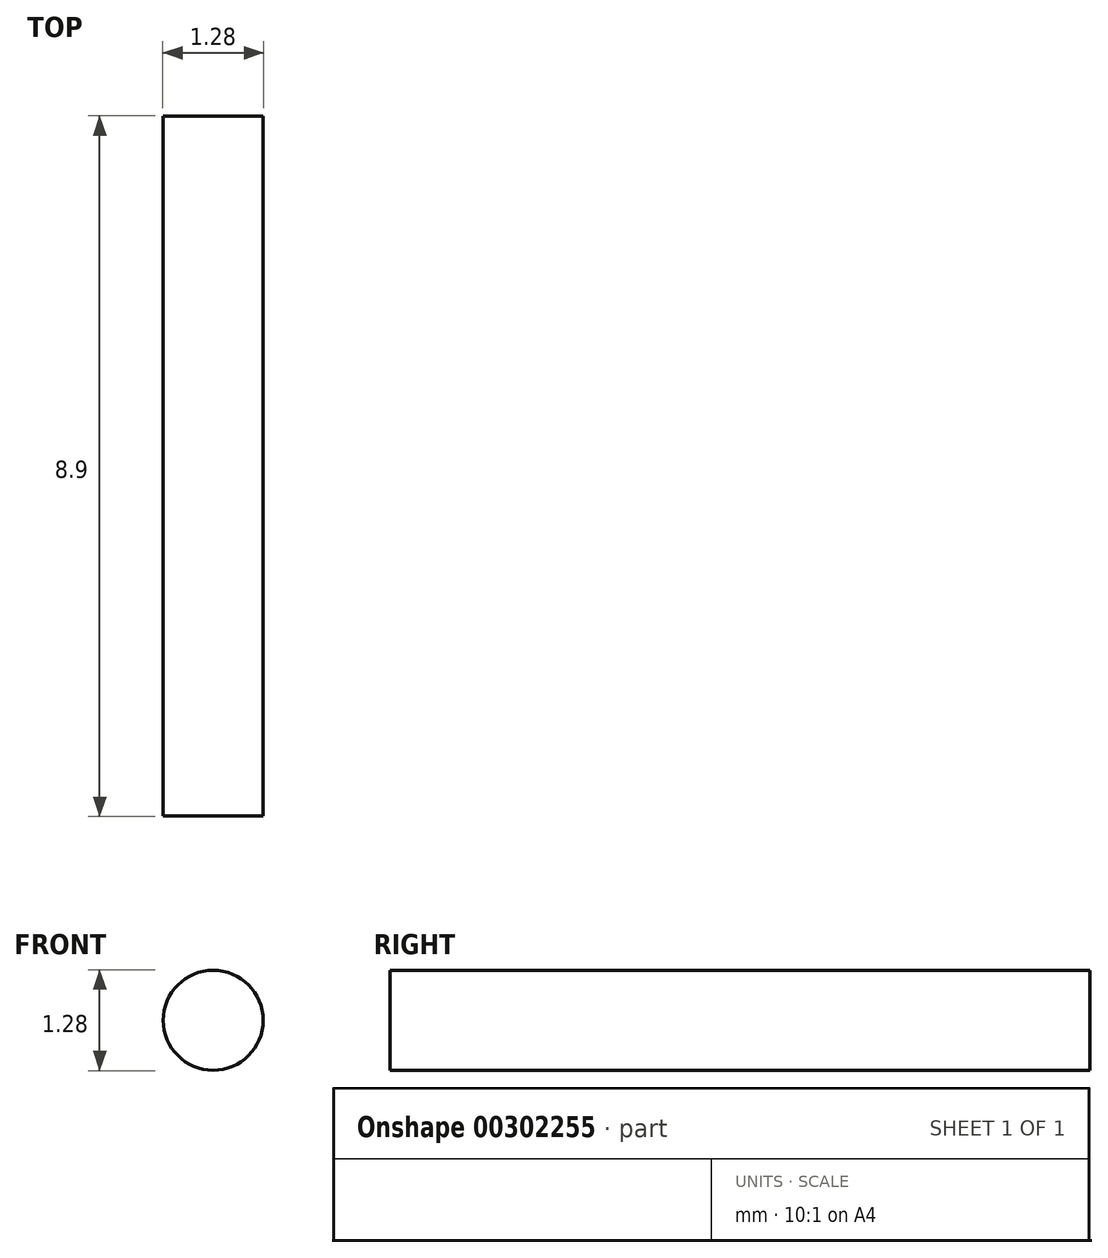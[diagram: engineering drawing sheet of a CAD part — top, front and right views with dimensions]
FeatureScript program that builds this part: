
annotation { "Feature Type Name" : "Feature", "Feature Type Description" : "" }
export const myFeature = defineFeature(function(context is Context, id is Id, definition is map)
    precondition{}
    {
        {
            var Q0;
            Q0=qCreatedBy(makeId("Front.planeOp"),FACE);
            var sketch = newSketch(context, id + "F0", { "sketchPlane" : qUnion([Q0])});
            skCircle(sketch, "E0", {"center": v(0, 0) * mm, "radius": 0.64 * mm});
            skSolve(sketch);
        }
        {
            var Q0;
            Q0 = qSketchRegion(id + "F0", true);
            extrude(context, id + "F1", {"entities" : qUnion([Q0]), "endBound" : BoundingType.SYMMETRIC, "depth" : 8.9 * mm});
        }
    });
